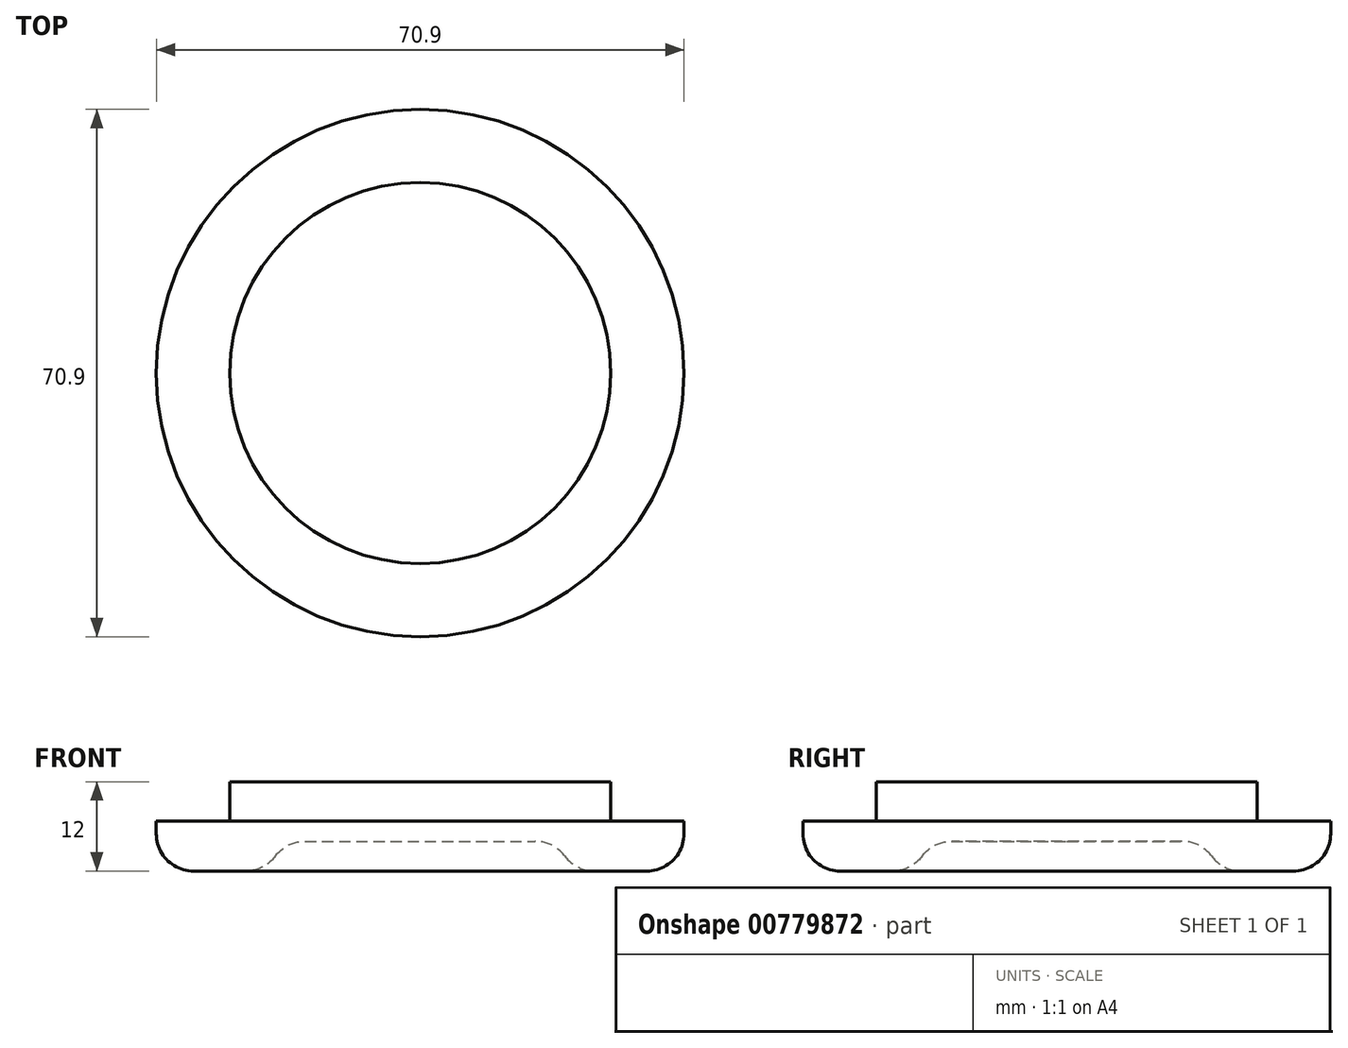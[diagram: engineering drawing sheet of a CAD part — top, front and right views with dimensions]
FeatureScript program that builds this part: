
annotation { "Feature Type Name" : "Feature", "Feature Type Description" : "" }
export const myFeature = defineFeature(function(context is Context, id is Id, definition is map)
    precondition{}
    {
        {
            var Q0;
            Q0=qCreatedBy(makeId("Top.planeOp"),FACE);
            var sketch = newSketch(context, id + "F0", { "sketchPlane" : qUnion([Q0])});
            skCircle(sketch, "E0", {"center": v(0, 0) * mm, "radius": 35.45 * mm});
            skCircle(sketch, "E1", {"center": v(0, 0) * mm, "radius": 26.6 * mm});
            skSolve(sketch);
        }
        {
            var Q0;
            Q0=makeQuery(id+"F0.imprint","IMPRINT",FACE,{"disambiguationData":[TD([[makeQuery(id+"F0.imprint","IMPRINT",EDGE,{"derivedFrom":sQuery(id+"F0.wireOp",EDGE,"E1")}),1.0]])]});
            var Q1;
            Q1=makeQuery(id+"F0.imprint","IMPRINT",FACE,{"disambiguationData":[TD([[makeQuery(id+"F0.imprint","IMPRINT",EDGE,{"derivedFrom":sQuery(id+"F0.wireOp",EDGE,"E0")}),1.0]])]});
            extrude(context, id + "F1", {"entities" : qUnion([Q0, Q1]), "depth" : 12 * mm, "offsetDistance" : 25 * mm});
        }
        {
            var Q0;
            Q0=makeQuery(id+"F1.opExtrude","CAP_FACE",FACE,{"disambiguationData":[OSD([sQuery(id+"F0.wireOp",EDGE,"E0")])],"isStart":true});
            var sketch = newSketch(context, id + "F2", { "sketchPlane" : qUnion([Q0])});
            skCircle(sketch, "E2", {"center": v(0, 0) * mm, "radius": 20.36 * mm});
            skSolve(sketch);
        }
        {
            var Q0;
            Q0=makeQuery(id+"F2.imprint","IMPRINT",FACE,{"disambiguationData":[TD([[makeQuery(id+"F2.imprint","IMPRINT",EDGE,{"derivedFrom":sQuery(id+"F2.wireOp",EDGE,"E2")}),1.0]])]});
            extrude(context, id + "F3", {"entities" : qUnion([Q0]), "operationType" : NewBodyOperationType.REMOVE, "oppositeDirection" : true, "depth" : 4 * mm, "offsetDistance" : 25 * mm});
        }
        {
            var Q0;
            Q0=makeQuery(id+"F3.boolean.opBoolean","COPY",EDGE,{"derivedFrom":makeQuery(id+"F3.opExtrude","CAP_EDGE",EDGE,{"disambiguationData":[OSD([sQuery(id+"F2.wireOp",EDGE,"E2")])],"isStart":false})});
            fillet(context, id + "F4", {"entities" : qUnion([Q0]), "radius" : 5 * mm, "tangentPropagation" : true, "allowEdgeOverflow" : false});
        }
        {
            var Q0;
            Q0=makeQuery(id+"F4.opFillet","BLEND_EDGE",EDGE,{"blendedFrom":[makeQuery(id+"F3.boolean.opBoolean","COPY",EDGE,{"derivedFrom":makeQuery(id+"F3.opExtrude","CAP_EDGE",EDGE,{"disambiguationData":[OSD([sQuery(id+"F2.wireOp",EDGE,"E2")])],"isStart":false})}),makeQuery(id+"F1.opExtrude","CAP_FACE",FACE,{"disambiguationData":[OSD([sQuery(id+"F0.wireOp",EDGE,"E0")])],"isStart":true})],"blendedInto":[makeQuery(id+"F1.opExtrude","CAP_FACE",FACE,{"disambiguationData":[OSD([sQuery(id+"F0.wireOp",EDGE,"E0")])],"isStart":true})]});
            fillet(context, id + "F5", {"entities" : qUnion([Q0]), "radius" : 5 * mm, "tangentPropagation" : true, "allowEdgeOverflow" : false});
        }
        {
            var Q0;
            Q0=makeQuery(id+"F1.opExtrude","CAP_EDGE",EDGE,{"disambiguationData":[OSD([sQuery(id+"F0.wireOp",EDGE,"E0")])],"isStart":true});
            fillet(context, id + "F6", {"entities" : qUnion([Q0]), "radius" : 5 * mm, "tangentPropagation" : true, "allowEdgeOverflow" : false});
        }
        {
            var Q0;
            Q0=makeQuery(id+"F1.opExtrude","CAP_FACE",FACE,{"disambiguationData":[OSD([sQuery(id+"F0.wireOp",EDGE,"E0")])],"isStart":false});
            var sketch = newSketch(context, id + "F7", { "sketchPlane" : qUnion([Q0])});
            skCircle(sketch, "E3", {"center": v(0, 0) * mm, "radius": 25.6 * mm});
            skSolve(sketch);
        }
        {
            var Q0;
            Q0=makeQuery(id+"F7.imprint","IMPRINT",FACE,{"disambiguationData":[TD([[makeQuery(id+"F7.imprint","IMPRINT",EDGE,{"derivedFrom":sQuery(id+"F7.wireOp",EDGE,"E3")}),-1.0]])]});
            extrude(context, id + "F8", {"entities" : qUnion([Q0]), "operationType" : NewBodyOperationType.REMOVE, "oppositeDirection" : true, "depth" : 5.3 * mm, "offsetDistance" : 25 * mm});
        }
    });
